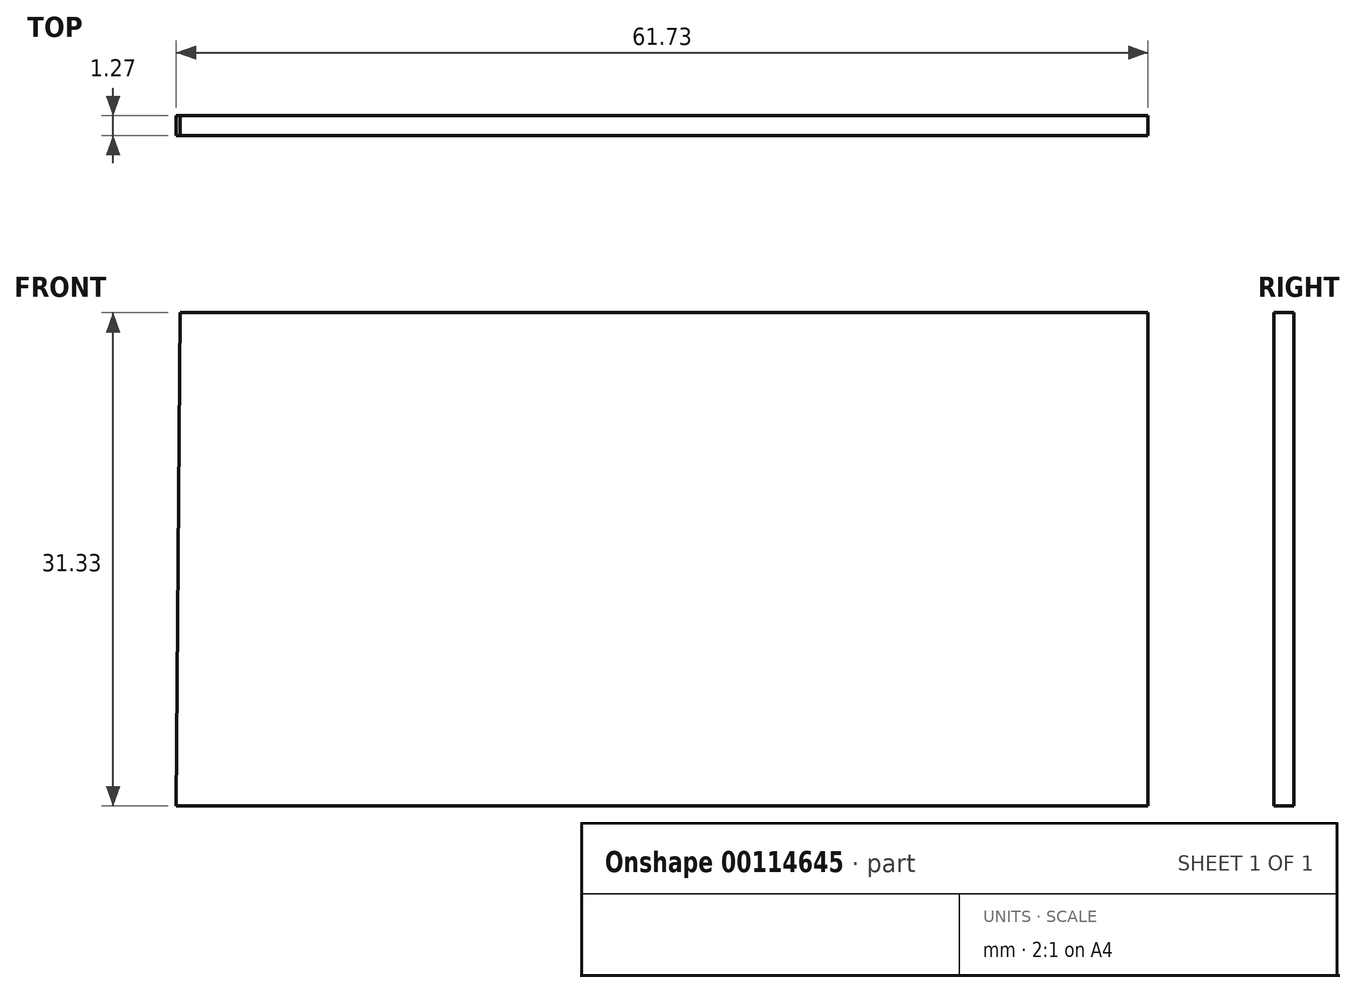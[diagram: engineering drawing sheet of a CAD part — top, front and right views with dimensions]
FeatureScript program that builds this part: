
annotation { "Feature Type Name" : "Feature", "Feature Type Description" : "" }
export const myFeature = defineFeature(function(context is Context, id is Id, definition is map)
    precondition{}
    {
        {
            var Q0;
            Q0=qCreatedBy(makeId("Front.planeOp"),FACE);
            var sketch = newSketch(context, id + "F0", { "sketchPlane" : qUnion([Q0])});
            skLineSegment(sketch, "E0", {"start": v(-61.5, 31.33) * mm, "end": v(0, 31.33) * mm});
            skLineSegment(sketch, "E1", {"start": v(0, 0) * mm, "end": v(-61.73, 0) * mm});
            skLineSegment(sketch, "E2", {"start": v(-61.73, 0) * mm, "end": v(-61.5, 31.33) * mm});
            skLineSegment(sketch, "E3", {"start": v(0, 31.33) * mm, "end": v(0, 0) * mm});
            skSolve(sketch);
        }
        {
            var Q0;
            Q0=makeQuery(id+"F0.imprint","IMPRINT",FACE,{"disambiguationData":[TD([[makeQuery(id+"F0.imprint","IMPRINT",EDGE,{"derivedFrom":sQuery(id+"F0.wireOp",EDGE,"E0")}),-1.0]])]});
            extrude(context, id + "F1", {"entities" : qUnion([Q0]), "depth" : 1.27 * mm});
        }
    });
